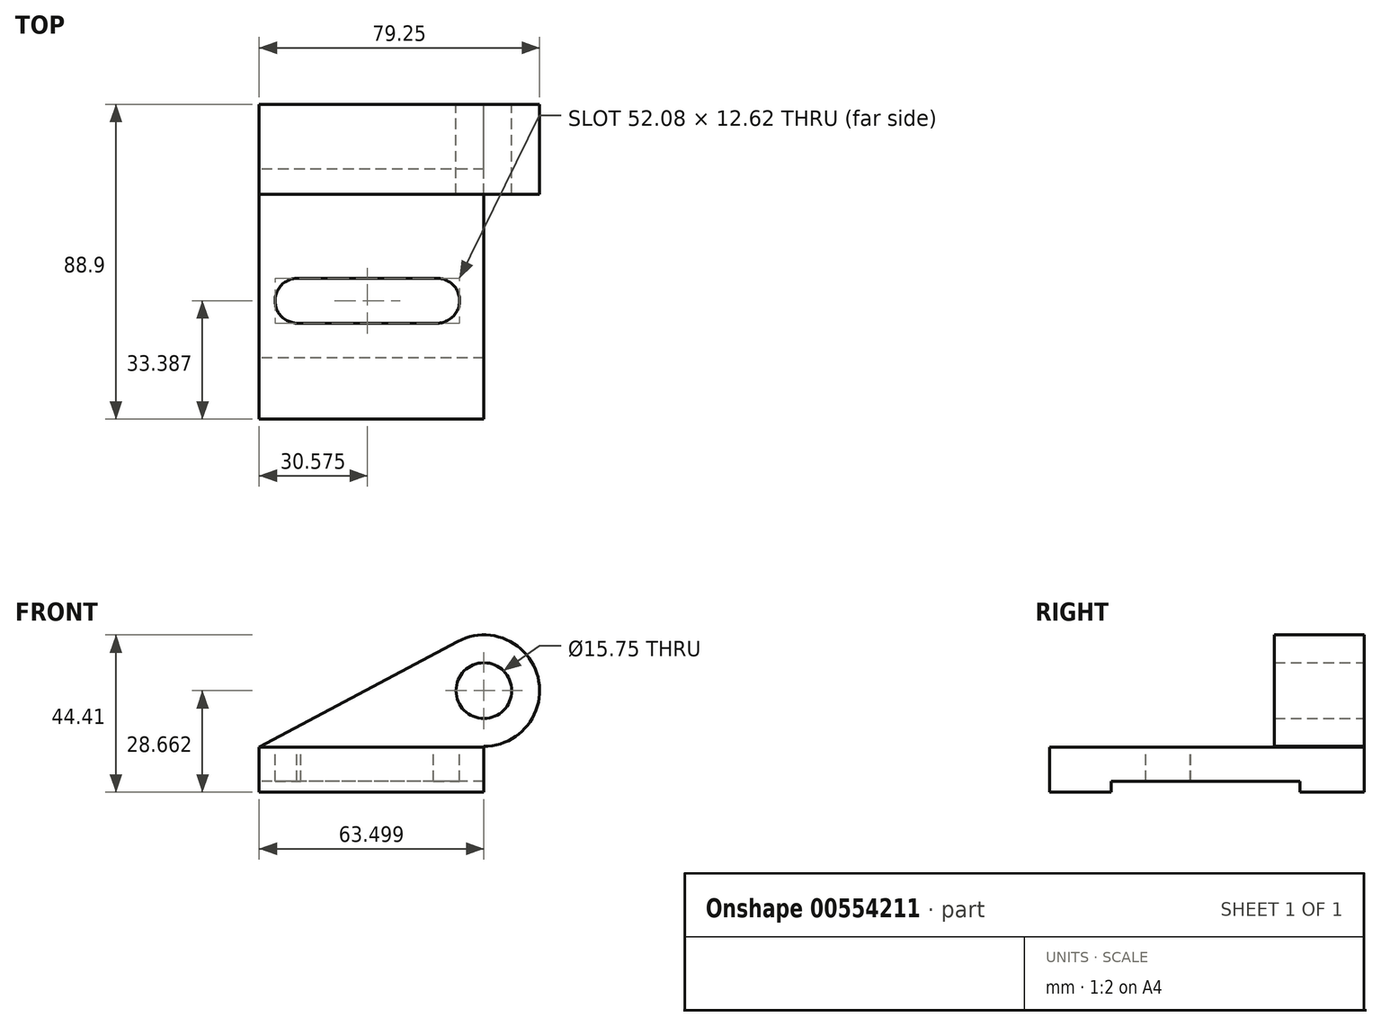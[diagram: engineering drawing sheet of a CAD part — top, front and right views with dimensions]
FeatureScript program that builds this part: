
annotation { "Feature Type Name" : "Feature", "Feature Type Description" : "" }
export const myFeature = defineFeature(function(context is Context, id is Id, definition is map)
    precondition{}
    {
        {
            var Q0;
            Q0=qCreatedBy(makeId("Front.planeOp"),FACE);
            var sketch = newSketch(context, id + "F0", { "sketchPlane" : qUnion([Q0])});
            skLineSegment(sketch, "E0", {"start": v(-45.96, 0) * mm, "end": v(17.54, 0) * mm});
            skLineSegment(sketch, "E1", {"start": v(-45.96, 0) * mm, "end": v(-45.96, 12.7) * mm});
            skLineSegment(sketch, "E2", {"start": v(-45.96, 12.7) * mm, "end": v(17.54, 12.7) * mm});
            skLineSegment(sketch, "E3", {"start": v(17.54, 12.7) * mm, "end": v(17.54, 0) * mm});
            skCircle(sketch, "E4", {"center": v(17.54, 28.66) * mm, "radius": 15.75 * mm});
            skLineSegment(sketch, "E5", {"start": v(-45.96, 12.7) * mm, "end": v(10.14, 42.56) * mm});
            skLineSegment(sketch, "E6", {"start": v(10.14, 42.56) * mm, "end": v(17.54, 12.7) * mm});
            skCircle(sketch, "E7", {"center": v(17.54, 28.66) * mm, "radius": 7.87 * mm});
            skSolve(sketch);
        }
        {
            var Q0;
            Q0=makeQuery(id+"F0.imprint","IMPRINT",FACE,{"disambiguationData":[TD([[makeQuery(id+"F0.imprint","IMPRINT",EDGE,{"derivedFrom":sQuery(id+"F0.wireOp",EDGE,"E0")}),1.0]])]});
            var Q1;
            {var subQ0=sQuery(id+"F0.wireOp",EDGE,"E2");Q1=makeQuery(id+"F0.imprint","IMPRINT",FACE,{"disambiguationData":[TD([[makeQuery(id+"F0.imprint","IMPRINT",EDGE,{"derivedFrom":subQ0}),1.0]])]});}
            var Q2;
            {var subQ0=sQuery(id+"F0.wireOp",EDGE,"E6");var subQ1=sQuery(id+"F0.wireOp",EDGE,"E4");var subQ3=makeQuery(id+"F0.imprint","INTERSECT",VERTEX,{"derivedFrom":[subQ1,subQ0]});Q2=makeQuery(id+"F0.imprint","IMPRINT",FACE,{"disambiguationData":[TD([[makeQuery(id+"F0.imprint","IMPRINT",EDGE,{"disambiguationData":[TD([[subQ3,1.0]])],"derivedFrom":subQ0}),-1.0]])]});}
            var Q3;
            {var subQ0=sQuery(id+"F0.wireOp",EDGE,"E6");var subQ1=sQuery(id+"F0.wireOp",EDGE,"E4");var subQ3=makeQuery(id+"F0.imprint","INTERSECT",VERTEX,{"derivedFrom":[subQ1,subQ0]});Q3=makeQuery(id+"F0.imprint","IMPRINT",FACE,{"disambiguationData":[TD([[makeQuery(id+"F0.imprint","IMPRINT",EDGE,{"disambiguationData":[TD([[subQ3,1.0]])],"derivedFrom":subQ0}),1.0]])]});}
            extrude(context, id + "F1", {"entities" : qUnion([Q0, Q1, Q2, Q3]), "depth" : 25.4 * mm, "offsetDistance" : 25.4 * mm});
        }
        {
            var Q0;
            Q0=makeQuery(id+"F1.opExtrude","CAP_FACE",FACE,{"disambiguationData":[OSD([sQuery(id+"F0.wireOp",EDGE,"E0"),sQuery(id+"F0.wireOp",EDGE,"E1"),sQuery(id+"F0.wireOp",EDGE,"E3"),sQuery(id+"F0.wireOp",EDGE,"E4"),sQuery(id+"F0.wireOp",EDGE,"E5"),sQuery(id+"F0.wireOp",EDGE,"E6"),sQuery(id+"F0.wireOp",EDGE,"E7")])],"isStart":false});
            var sketch = newSketch(context, id + "F2", { "sketchPlane" : qUnion([Q0])});
            skLineSegment(sketch, "E8", {"start": v(-45.96, 12.7) * mm, "end": v(17.54, 12.7) * mm});
            skSolve(sketch);
        }
        {
            var Q0;
            Q0=makeQuery(id+"F2.imprint","IMPRINT",FACE,{"disambiguationData":[TD([[makeQuery(id+"F2.imprint","IMPRINT",EDGE,{"derivedFrom":sQuery(id+"F2.wireOp",EDGE,"E8")}),-1.0]])]});
            extrude(context, id + "F3", {"entities" : qUnion([Q0]), "operationType" : NewBodyOperationType.ADD, "depth" : 63.5 * mm, "offsetDistance" : 25.4 * mm});
        }
        {
            var Q0;
            {var subQ0=sQuery(id+"F0.wireOp",EDGE,"E0");Q0=makeQuery(id+"F3.boolean.opBoolean","MERGE",FACE,{"derivedFrom":[makeQuery(id+"F1.opExtrude","SWEPT_FACE",FACE,{"disambiguationData":[OSD([subQ0])]}),makeQuery(id+"F3.opExtrude","SWEPT_FACE",FACE,{"disambiguationData":[OSD([subQ0])]})]});}
            var sketch = newSketch(context, id + "F4", { "sketchPlane" : qUnion([Q0])});
            skLineSegment(sketch, "E9", {"start": v(17.54, 71.6) * mm, "end": v(-45.96, 71.6) * mm});
            skLineSegment(sketch, "E10", {"start": v(17.54, 18.25) * mm, "end": v(-45.96, 18.25) * mm});
            skSolve(sketch);
        }
        {
            var Q0;
            {var subQ0=sQuery(id+"F4.wireOp",EDGE,"E9");Q0=makeQuery(id+"F4.imprint","IMPRINT",FACE,{"disambiguationData":[TD([[makeQuery(id+"F4.imprint","IMPRINT",EDGE,{"derivedFrom":subQ0}),1.0]])]});}
            extrude(context, id + "F5", {"entities" : qUnion([Q0]), "operationType" : NewBodyOperationType.REMOVE, "oppositeDirection" : true, "depth" : 3.05 * mm, "offsetDistance" : 25.4 * mm});
        }
        {
            var Q0;
            Q0=makeQuery(id+"F3.opExtrude","SWEPT_FACE",FACE,{"disambiguationData":[OSD([sQuery(id+"F2.wireOp",EDGE,"E8")])]});
            var sketch = newSketch(context, id + "F6", { "sketchPlane" : qUnion([Q0])});
            skCircle(sketch, "E11", {"center": v(-35.1, -55.48) * mm, "radius": 6.35 * mm});
            skCircle(sketch, "E12", {"center": v(4.33, -55.47) * mm, "radius": 6.35 * mm});
            skLineSegment(sketch, "E13", {"start": v(-34.14, -49.2) * mm, "end": v(3.33, -49.2) * mm});
            skLineSegment(sketch, "E14", {"start": v(-35.27, -61.83) * mm, "end": v(4.33, -61.82) * mm});
            skSolve(sketch);
        }
        {
            var Q0;
            {var subQ0=sQuery(id+"F6.wireOp",EDGE,"E13");Q0=makeQuery(id+"F6.imprint","IMPRINT",FACE,{"disambiguationData":[TD([[makeQuery(id+"F6.imprint","IMPRINT",EDGE,{"derivedFrom":subQ0}),-1.0]])]});}
            var Q1;
            {var subQ0=sQuery(id+"F6.wireOp",EDGE,"E11");var subQ1=makeQuery(id+"F6.imprint","INTERSECT",VERTEX,{"derivedFrom":[subQ0,sQuery(id+"F6.wireOp",EDGE,"E13")]});Q1=makeQuery(id+"F6.imprint","IMPRINT",FACE,{"disambiguationData":[TD([[makeQuery(id+"F6.imprint","IMPRINT",EDGE,{"disambiguationData":[TD([[subQ1,-1.0]])],"derivedFrom":subQ0}),1.0]])]});}
            var Q2;
            {var subQ0=sQuery(id+"F6.wireOp",EDGE,"E12");var subQ1=makeQuery(id+"F6.imprint","INTERSECT",VERTEX,{"derivedFrom":[subQ0,sQuery(id+"F6.wireOp",EDGE,"E13")]});Q2=makeQuery(id+"F6.imprint","IMPRINT",FACE,{"disambiguationData":[TD([[makeQuery(id+"F6.imprint","IMPRINT",EDGE,{"disambiguationData":[TD([[subQ1,-1.0]])],"derivedFrom":subQ0}),1.0]])]});}
            extrude(context, id + "F7", {"entities" : qUnion([Q0, Q1, Q2]), "operationType" : NewBodyOperationType.REMOVE, "oppositeDirection" : true, "depth" : 25.4 * mm, "offsetDistance" : 25.4 * mm});
        }
    });
